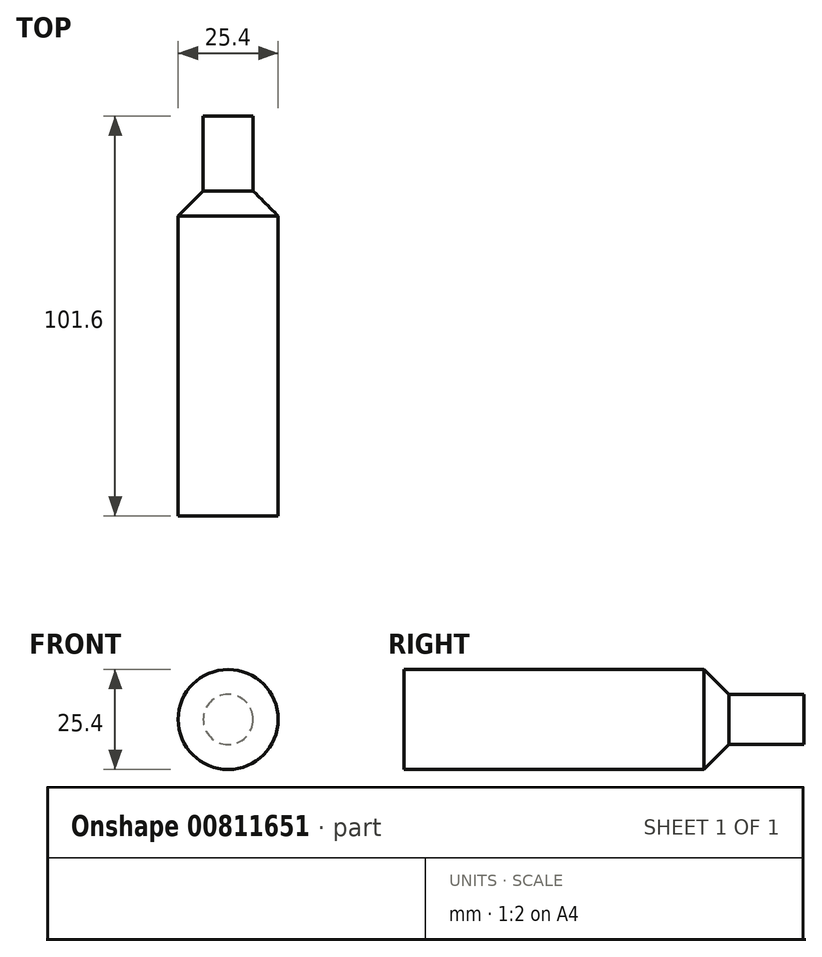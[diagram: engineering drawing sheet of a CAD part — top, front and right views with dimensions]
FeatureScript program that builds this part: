
annotation { "Feature Type Name" : "Feature", "Feature Type Description" : "" }
export const myFeature = defineFeature(function(context is Context, id is Id, definition is map)
    precondition{}
    {
        {
            var Q0;
            Q0=qCreatedBy(makeId("Top.planeOp"),FACE);
            var sketch = newSketch(context, id + "F0", { "sketchPlane" : qUnion([Q0])});
            skLineSegment(sketch, "E0.bottom", {"start": v(-13.65, 3.72) * mm, "end": v(11.75, 3.72) * mm});
            skLineSegment(sketch, "E0.top", {"start": v(-13.65, -72.48) * mm, "end": v(11.75, -72.48) * mm});
            skLineSegment(sketch, "E0.left", {"start": v(-13.65, 3.72) * mm, "end": v(-13.65, -72.48) * mm});
            skLineSegment(sketch, "E0.right", {"start": v(11.75, 3.72) * mm, "end": v(11.75, -72.48) * mm});
            skLineSegment(sketch, "E1", {"start": v(-13.65, 3.72) * mm, "end": v(-7.3, 10.07) * mm});
            skLineSegment(sketch, "E2", {"start": v(-7.3, 10.07) * mm, "end": v(5.4, 10.07) * mm});
            skLineSegment(sketch, "E3", {"start": v(5.4, 10.07) * mm, "end": v(11.75, 3.72) * mm});
            skLineSegment(sketch, "E4", {"start": v(-7.3, 10.07) * mm, "end": v(-7.3, 29.12) * mm});
            skLineSegment(sketch, "E5", {"start": v(5.4, 10.07) * mm, "end": v(5.4, 29.12) * mm});
            skLineSegment(sketch, "E6", {"start": v(-7.3, 29.12) * mm, "end": v(5.4, 29.12) * mm});
            skLineSegment(sketch, "E7", {"start": v(-13.65, -72.48) * mm, "end": v(-0.95, -72.48) * mm});
            skLineSegment(sketch, "E8", {"start": v(-0.95, -72.48) * mm, "end": v(-0.95, 3.72) * mm});
            skLineSegment(sketch, "E9", {"start": v(-0.95, 3.72) * mm, "end": v(-0.95, 29.12) * mm});
            skSolve(sketch);
        }
        {
            var Q0;
            {var subQ2=sQuery(id+"F0.wireOp",EDGE,"E0.left");Q0=makeQuery(id+"F0.imprint","IMPRINT",FACE,{"disambiguationData":[TD([[makeQuery(id+"F0.imprint","IMPRINT",EDGE,{"derivedFrom":subQ2}),1.0]])]});}
            var Q1;
            Q1=sQuery(id+"F0.wireOp",EDGE,"E8");
            revolve(context, id + "F1", {"surfaceOperationType" : NewSurfaceOperationType.NEW, "entities" : qUnion([Q0]), "axis" : qUnion([Q1]), "revolveType" : RevolveType.FULL});
        }
        {
            var Q0;
            {var subQ3=sQuery(id+"F0.wireOp",EDGE,"E1");Q0=makeQuery(id+"F0.imprint","IMPRINT",FACE,{"disambiguationData":[TD([[makeQuery(id+"F0.imprint","IMPRINT",EDGE,{"derivedFrom":subQ3}),-1.0]])]});}
            var Q1;
            Q1=sQuery(id+"F0.wireOp",EDGE,"E9");
            revolve(context, id + "F2", {"operationType" : NewBodyOperationType.ADD, "surfaceOperationType" : NewSurfaceOperationType.NEW, "entities" : qUnion([Q0]), "axis" : qUnion([Q1]), "revolveType" : RevolveType.FULL});
        }
        {
            var Q0;
            {var subQ0=sQuery(id+"F0.wireOp",EDGE,"E4");Q0=makeQuery(id+"F0.imprint","IMPRINT",FACE,{"disambiguationData":[TD([[makeQuery(id+"F0.imprint","IMPRINT",EDGE,{"derivedFrom":subQ0}),-1.0]])]});}
            var Q1;
            Q1=sQuery(id+"F0.wireOp",EDGE,"E9");
            revolve(context, id + "F3", {"operationType" : NewBodyOperationType.ADD, "surfaceOperationType" : NewSurfaceOperationType.NEW, "entities" : qUnion([Q0]), "axis" : qUnion([Q1]), "revolveType" : RevolveType.FULL});
        }
    });
